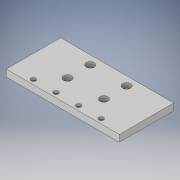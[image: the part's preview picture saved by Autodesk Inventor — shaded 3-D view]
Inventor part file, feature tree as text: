
AUTODESK INVENTOR PART (.ipt)
format: ipt  version: 2019 (Build 230136000, 136)  size: 142,336 bytes
history: native  units: mm
features: sketch x3, hole x2, extrude x1, projected_geometry x1
ambient origin geometry x8: Origin, YZ Plane, XZ Plane, XY Plane, X Axis, Y Axis, Z Axis, Center Point
bodies: Solid1 (feature_tree)
feature tree (7):
  extrude  "Extrusion1"  Depth=76.0mm
  hole  "Hole1"  [1 undecoded]
  hole  "Hole2"  [1 undecoded]
  sketch  "Sketch1"  dims[d0=158.0mm d1=76.0mm]
  sketch  "Sketch2"  dims[d2=9.525mm d3=0.0mm d4=50.8mm]
  projected_geometry  "Projected Loop1"
  sketch  "Sketch3"  dims[d5=50.8mm d6=31.75mm d8=6.756mm d9=6.0mm d10=11.113mm d11=6.35mm d12=90.0deg d13=8.0mm d14=20.594885mm d16=32.0mm d17=6.35mm d19=31.6mm d20=31.6mm d21=31.6mm d22=31.6mm d23=31.6mm d24=6.756mm d25=6.0mm d26=11.113mm d27=6.35mm d28=90.0deg d29=8.0mm d30=20.594885mm]
note: 2 required parameter values undecoded (feature->parameter linkage not recoverable at this tier; creation-order binding heuristic only, values carry confidence <= 0.55)
